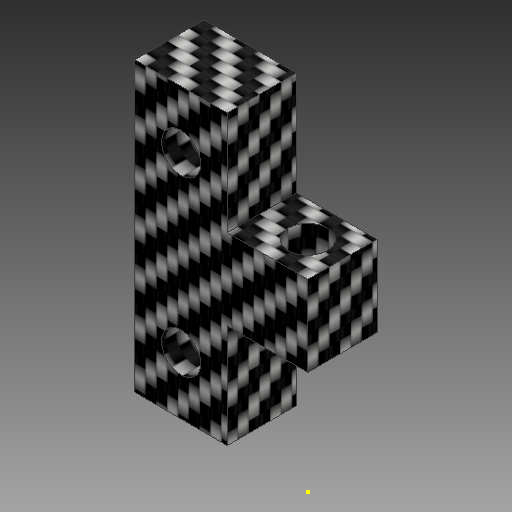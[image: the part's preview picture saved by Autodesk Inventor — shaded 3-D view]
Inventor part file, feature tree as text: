
AUTODESK INVENTOR PART (.ipt)
format: ipt  version: 2018 (Build 220112000, 112)  size: 229,376 bytes
history: native  units: mm
features: sketch x5, extrude x4
ambient origin geometry x8: Origin, YZ Plane, XZ Plane, XY Plane, X Axis, Y Axis, Z Axis, Center Point
bodies: Volumenkörper1 (feature_tree)
feature tree (9):
  extrude  "Extrusion1"  Depth=15.0mm
  sketch  "Skizze3"  dims[d2=6.0mm d3=0.0mm d11=3.4mm]
  extrude  "Extrusion4"  Depth=6.0mm
  extrude  "Extrusion5"  Depth=5.0mm
  extrude  "Extrusion6"  Depth=4.0mm
  sketch  "Skizze1"  dims[d0=25.0mm d1=15.0mm]
  sketch  "Skizze6"  dims[d12=4.0mm d13=5.0mm]
  sketch  "Skizze7"  dims[d14=3.4mm d15=4.0mm]
  sketch  "Skizze8"  dims[d16=5.0mm d17=30.0mm d18=0.0mm d19=7.0mm d20=9.0mm d21=7.0mm d22=9.0mm d23=30.0mm d24=0.0mm d25=3.4mm d26=3.0mm d27=3.0mm d28=30.0mm d29=0.0mm]
